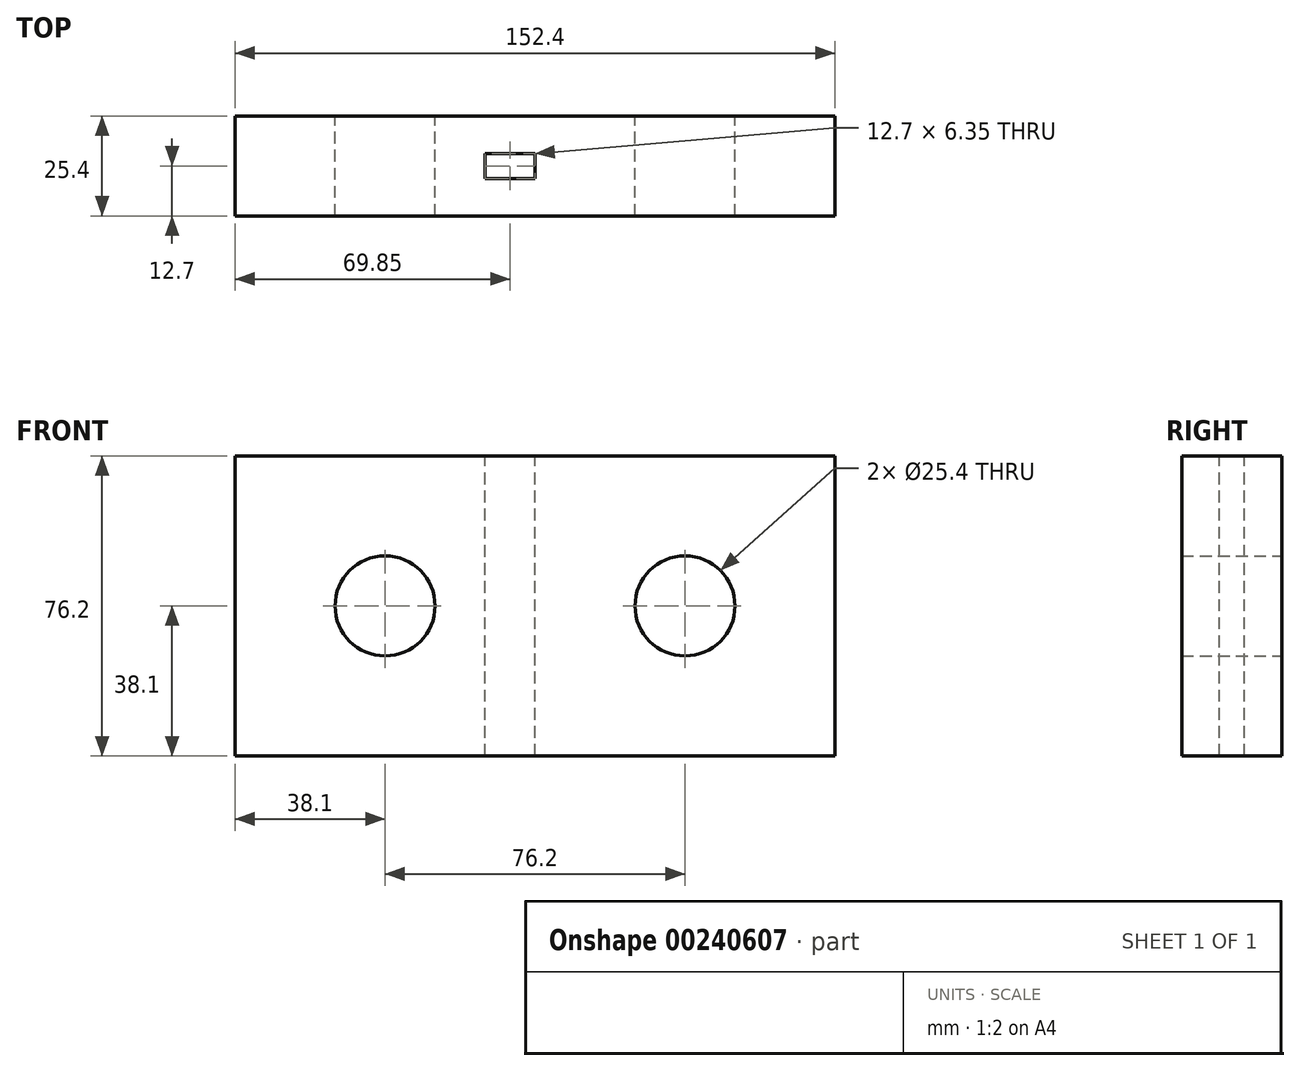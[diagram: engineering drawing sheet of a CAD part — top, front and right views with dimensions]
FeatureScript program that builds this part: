
annotation { "Feature Type Name" : "Feature", "Feature Type Description" : "" }
export const myFeature = defineFeature(function(context is Context, id is Id, definition is map)
    precondition{}
    {
        {
            var Q0;
            Q0=qCreatedBy(makeId("Front.planeOp"),FACE);
            var sketch = newSketch(context, id + "F0", { "sketchPlane" : qUnion([Q0])});
            skLineSegment(sketch, "E0.bottom", {"start": v(76.2, 38.1) * mm, "end": v(-76.2, 38.1) * mm});
            skLineSegment(sketch, "E0.top", {"start": v(76.2, -38.1) * mm, "end": v(-76.2, -38.1) * mm});
            skLineSegment(sketch, "E0.left", {"start": v(76.2, 38.1) * mm, "end": v(76.2, -38.1) * mm});
            skLineSegment(sketch, "E0.right", {"start": v(-76.2, 38.1) * mm, "end": v(-76.2, -38.1) * mm});
            skPoint(sketch, "E0.middle", {"position": v(0, 0) * mm});
            skCircle(sketch, "E1", {"center": v(-38.1, 0) * mm, "radius": 12.7 * mm});
            skCircle(sketch, "E2.MirrorC", {"center": v(38.1, 0) * mm, "radius": 12.7 * mm});
            skSolve(sketch);
        }
        {
            var Q0;
            Q0=makeQuery(id+"F0.imprint","IMPRINT",FACE,{"disambiguationData":[TD([[makeQuery(id+"F0.imprint","IMPRINT",EDGE,{"derivedFrom":sQuery(id+"F0.wireOp",EDGE,"E0.bottom")}),1.0]])]});
            extrude(context, id + "F1", {"entities" : qUnion([Q0]), "depth" : 25.4 * mm});
        }
        {
            var Q0;
            Q0=makeQuery(id+"F1.opExtrude","SWEPT_FACE",FACE,{"disambiguationData":[OSD([sQuery(id+"F0.wireOp",EDGE,"E0.bottom")])]});
            var sketch = newSketch(context, id + "F2", { "sketchPlane" : qUnion([Q0])});
            skLineSegment(sketch, "E3.bottom", {"start": v(0, -9.53) * mm, "end": v(-12.7, -9.53) * mm});
            skLineSegment(sketch, "E3.top", {"start": v(0, -15.88) * mm, "end": v(-12.7, -15.88) * mm});
            skLineSegment(sketch, "E3.left", {"start": v(0, -9.53) * mm, "end": v(0, -15.88) * mm});
            skLineSegment(sketch, "E3.right", {"start": v(-12.7, -9.53) * mm, "end": v(-12.7, -15.88) * mm});
            skSolve(sketch);
        }
        {
            var Q0;
            Q0=makeQuery(id+"F2.imprint","IMPRINT",FACE,{"disambiguationData":[TD([[makeQuery(id+"F2.imprint","IMPRINT",EDGE,{"derivedFrom":sQuery(id+"F2.wireOp",EDGE,"E3.bottom")}),1.0]])]});
            extrude(context, id + "F3", {"entities" : qUnion([Q0]), "operationType" : NewBodyOperationType.REMOVE, "endBound" : BoundingType.THROUGH_ALL, "oppositeDirection" : true, "depth" : 25.4 * mm});
        }
    });
